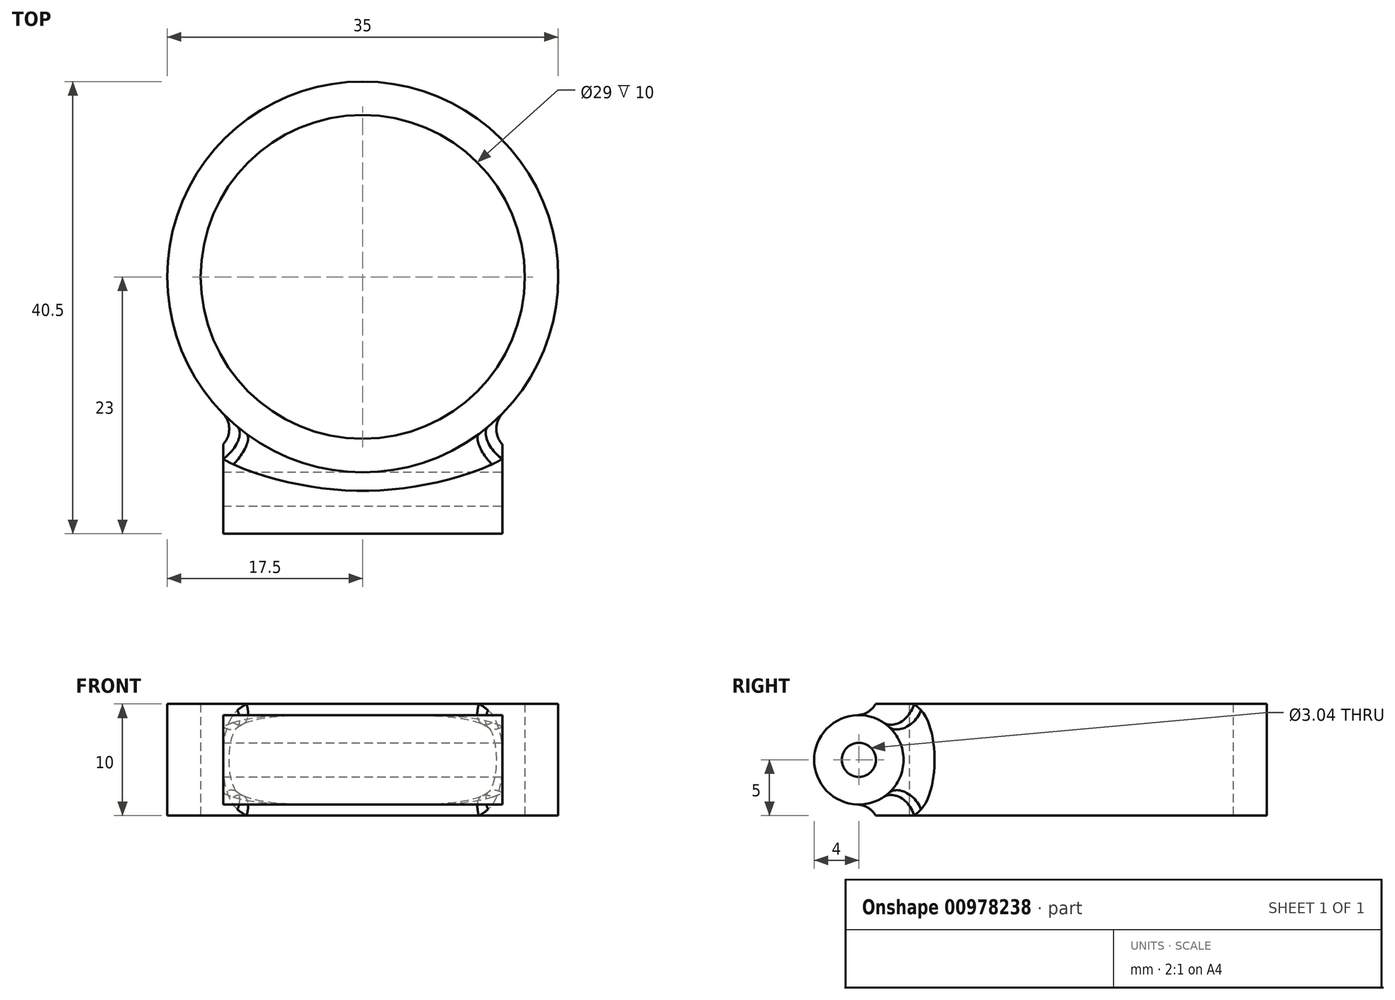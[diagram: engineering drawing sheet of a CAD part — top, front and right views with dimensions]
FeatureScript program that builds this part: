
annotation { "Feature Type Name" : "Feature", "Feature Type Description" : "" }
export const myFeature = defineFeature(function(context is Context, id is Id, definition is map)
    precondition{}
    {
        {
            var Q0;
            Q0=qCreatedBy(makeId("Top.planeOp"),FACE);
            var sketch = newSketch(context, id + "F0", { "sketchPlane" : qUnion([Q0])});
            skCircle(sketch, "E0", {"center": v(0, 0) * mm, "radius": 17.5 * mm});
            skCircle(sketch, "E1", {"center": v(0, 0) * mm, "radius": 14.5 * mm});
            skSolve(sketch);
        }
        {
            var Q0;
            Q0=makeQuery(id+"F0.imprint","IMPRINT",FACE,{"disambiguationData":[TD([[makeQuery(id+"F0.imprint","IMPRINT",EDGE,{"derivedFrom":sQuery(id+"F0.wireOp",EDGE,"E0")}),1.0]])]});
            extrude(context, id + "F1", {"entities" : qUnion([Q0]), "depth" : 10 * mm, "offsetDistance" : 25 * mm});
        }
        {
            var Q0;
            Q0=qCreatedBy(makeId("Right.planeOp"),FACE);
            var sketch = newSketch(context, id + "F2", { "sketchPlane" : qUnion([Q0])});
            skLineSegment(sketch, "E2", {"start": v(-19, 0) * mm, "end": v(-19, 31.86) * mm, "construction": true});
            skCircle(sketch, "E3", {"center": v(-19, 5) * mm, "radius": 4 * mm});
            skSolve(sketch);
        }
        {
            var Q0;
            Q0 = qSketchRegion(id + "F2", true);
            extrude(context, id + "F3", {"entities" : qUnion([Q0]), "operationType" : NewBodyOperationType.ADD, "endBound" : BoundingType.SYMMETRIC, "depth" : 25 * mm, "offsetDistance" : 25 * mm});
        }
        {
            var Q0;
            Q0=makeQuery(id+"F3.boolean.opBoolean","INTERSECT",EDGE,{"derivedFrom":[makeQuery(id+"F1.opExtrude","SWEPT_FACE",FACE,{"disambiguationData":[OSD([sQuery(id+"F0.wireOp",EDGE,"E0")])]}),makeQuery(id+"F3.opExtrude","SWEPT_FACE",FACE,{"disambiguationData":[OSD([sQuery(id+"F2.wireOp",EDGE,"E3")])]})]});
            fillet(context, id + "F4", {"entities" : qUnion([Q0]), "radius" : 2 * mm, "tangentPropagation" : true, "allowEdgeOverflow" : false});
        }
        {
            var Q0;
            Q0=makeQuery(id+"F3.opExtrude","CAP_FACE",FACE,{"disambiguationData":[OSD([sQuery(id+"F2.wireOp",EDGE,"E3")])],"isStart":false});
            var sketch = newSketch(context, id + "F5", { "sketchPlane" : qUnion([Q0])});
            skCircle(sketch, "E4", {"center": v(-19, 5) * mm, "radius": 1.52 * mm});
            skSolve(sketch);
        }
        {
            var Q0;
            Q0=makeQuery(id+"F5.imprint","IMPRINT",FACE,{"disambiguationData":[TD([[makeQuery(id+"F5.imprint","IMPRINT",EDGE,{"derivedFrom":sQuery(id+"F5.wireOp",EDGE,"E4")}),1.0]])]});
            extrude(context, id + "F6", {"entities" : qUnion([Q0]), "operationType" : NewBodyOperationType.REMOVE, "endBound" : BoundingType.THROUGH_ALL, "oppositeDirection" : true, "depth" : 25 * mm, "offsetDistance" : 25 * mm});
        }
    });
